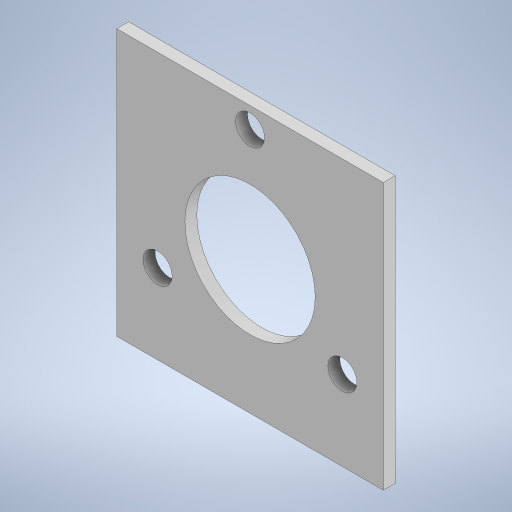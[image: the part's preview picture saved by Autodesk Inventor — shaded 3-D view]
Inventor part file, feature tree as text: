
AUTODESK INVENTOR PART (.ipt)
format: ipt  version: 2024 (Build 280153000, 153)  size: 240,128 bytes
history: native  units: in
note: dims shown in document units (in); Inventor stores cm internally (conversion verified against a paired STEP export)
features: extrude x1, sketch x1
ambient origin geometry x8: Origin, YZ Plane, XZ Plane, XY Plane, X Axis, Y Axis, Z Axis, Center Point
bodies: Body1 (feature_tree)
feature tree (2):
  extrude  "Extrusion2"  Depth=1.7717in
  sketch  "Sketch1"  dims[d0=1.7717in d1=1.7717in d2=0.8661in d3=0.748in d4=0.6142in d5=120.0deg d6=0.6142in d7=120.0deg d8=0.1929in d9=0.1929in d10=0.1929in d16=0.0787in d17=0.0in d11=0.0197in d12=0.0344in d13=0.0197in d14=0.0344in]
